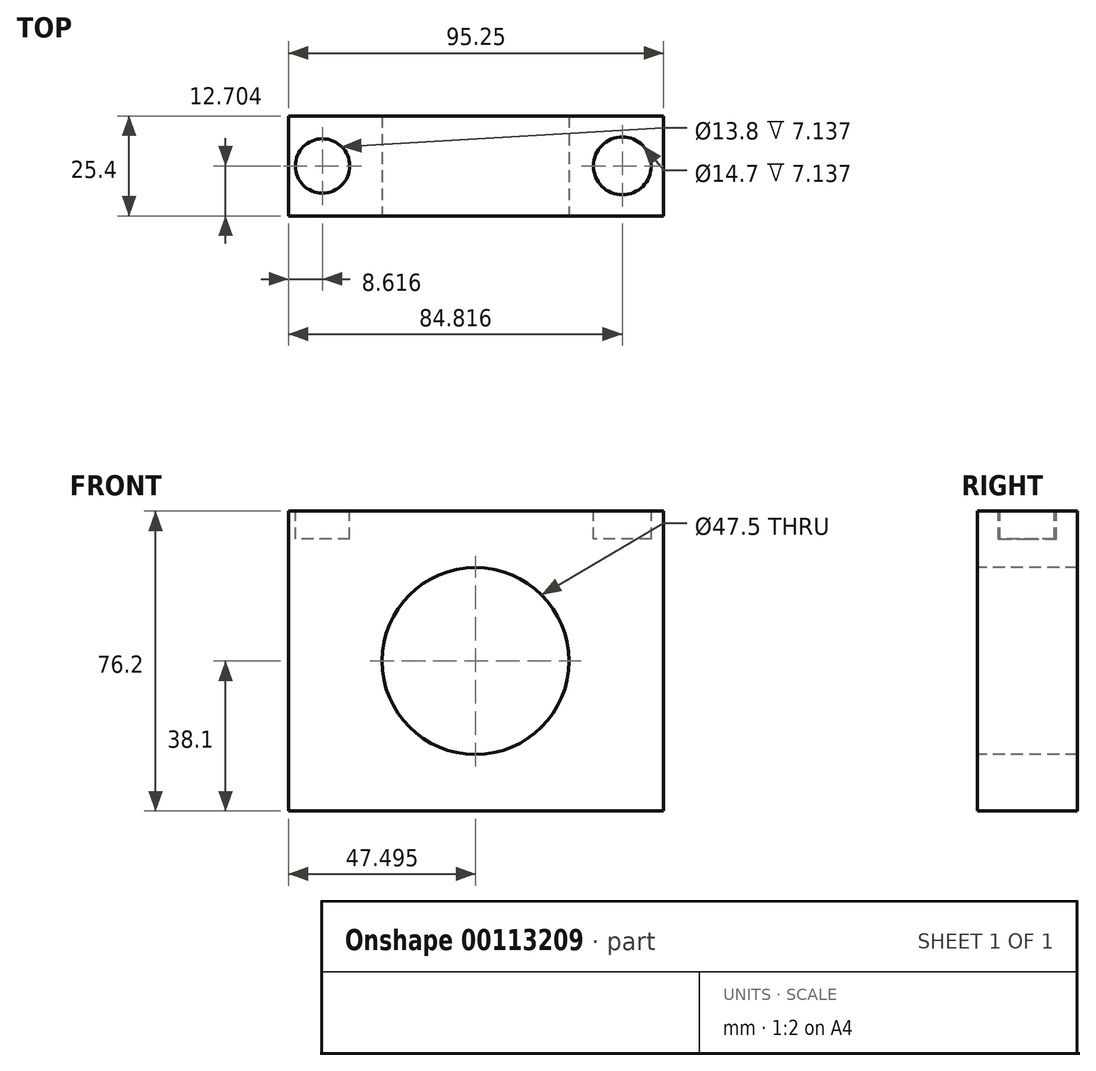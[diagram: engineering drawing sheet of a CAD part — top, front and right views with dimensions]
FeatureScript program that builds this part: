
annotation { "Feature Type Name" : "Feature", "Feature Type Description" : "" }
export const myFeature = defineFeature(function(context is Context, id is Id, definition is map)
    precondition{}
    {
        {
            var Q0;
            Q0=qCreatedBy(makeId("Top.planeOp"),FACE);
            var sketch = newSketch(context, id + "F0", { "sketchPlane" : qUnion([Q0])});
            skLineSegment(sketch, "E0.bottom", {"start": v(-48.71, -10.22) * mm, "end": v(46.54, -10.22) * mm});
            skLineSegment(sketch, "E0.top", {"start": v(-48.71, 15.18) * mm, "end": v(46.54, 15.18) * mm});
            skLineSegment(sketch, "E0.left", {"start": v(-48.71, -10.22) * mm, "end": v(-48.71, 15.18) * mm});
            skLineSegment(sketch, "E0.right", {"start": v(46.54, -10.22) * mm, "end": v(46.54, 15.18) * mm});
            skSolve(sketch);
        }
        {
            var Q0;
            Q0=makeQuery(id+"F0.imprint","IMPRINT",FACE,{"disambiguationData":[TD([[makeQuery(id+"F0.imprint","IMPRINT",EDGE,{"derivedFrom":sQuery(id+"F0.wireOp",EDGE,"E0.bottom")}),1.0]])]});
            extrude(context, id + "F1", {"entities" : qUnion([Q0]), "depth" : 76.2 * mm});
        }
        {
            var Q0;
            Q0=makeQuery(id+"F1.opExtrude","CAP_FACE",FACE,{"disambiguationData":[OSD([sQuery(id+"F0.wireOp",EDGE,"E0.bottom"),sQuery(id+"F0.wireOp",EDGE,"E0.top"),sQuery(id+"F0.wireOp",EDGE,"E0.left"),sQuery(id+"F0.wireOp",EDGE,"E0.right")])],"isStart":false});
            var sketch = newSketch(context, id + "F2", { "sketchPlane" : qUnion([Q0])});
            skCircle(sketch, "E1", {"center": v(-40.1, 2.48) * mm, "radius": 6.9 * mm});
            skPoint(sketch, "E1.centerSnap0", {"position": v(-48.71, 2.48) * mm});
            skCircle(sketch, "E2", {"center": v(36.1, 2.48) * mm, "radius": 7.35 * mm});
            skPoint(sketch, "E2.centerSnap0", {"position": v(46.54, 2.48) * mm});
            skSolve(sketch);
        }
        {
            var Q0;
            Q0=makeQuery(id+"F2.imprint","IMPRINT",FACE,{"disambiguationData":[TD([[makeQuery(id+"F2.imprint","IMPRINT",EDGE,{"derivedFrom":sQuery(id+"F2.wireOp",EDGE,"E2")}),1.0]])]});
            var Q1;
            Q1=makeQuery(id+"F2.imprint","IMPRINT",FACE,{"disambiguationData":[TD([[makeQuery(id+"F2.imprint","IMPRINT",EDGE,{"derivedFrom":sQuery(id+"F2.wireOp",EDGE,"E1")}),1.0]])]});
            extrude(context, id + "F3", {"entities" : qUnion([Q0, Q1]), "operationType" : NewBodyOperationType.REMOVE, "oppositeDirection" : true, "depth" : 7.14 * mm});
        }
        {
            var Q0;
            Q0=makeQuery(id+"F1.opExtrude","SWEPT_FACE",FACE,{"disambiguationData":[OSD([sQuery(id+"F0.wireOp",EDGE,"E0.bottom")])]});
            var sketch = newSketch(context, id + "F4", { "sketchPlane" : qUnion([Q0])});
            skPoint(sketch, "E3.centerSnap0", {"position": v(-48.71, 38.1) * mm});
            skLineSegment(sketch, "E4", {"start": v(46.54, 0) * mm, "end": v(46.54, 38.1) * mm, "construction": true});
            skLineSegment(sketch, "E5", {"start": v(46.54, 38.1) * mm, "end": v(-1.21, 38.1) * mm, "construction": true});
            skCircle(sketch, "E6", {"center": v(-1.21, 38.1) * mm, "radius": 23.75 * mm});
            skSolve(sketch);
        }
        {
            var Q0;
            Q0=makeQuery(id+"F4.imprint","IMPRINT",FACE,{"disambiguationData":[TD([[makeQuery(id+"F4.imprint","IMPRINT",EDGE,{"derivedFrom":sQuery(id+"F4.wireOp",EDGE,"E6")}),1.0]])]});
            extrude(context, id + "F5", {"entities" : qUnion([Q0]), "operationType" : NewBodyOperationType.REMOVE, "oppositeDirection" : true, "depth" : 35.1 * mm});
        }
    });
